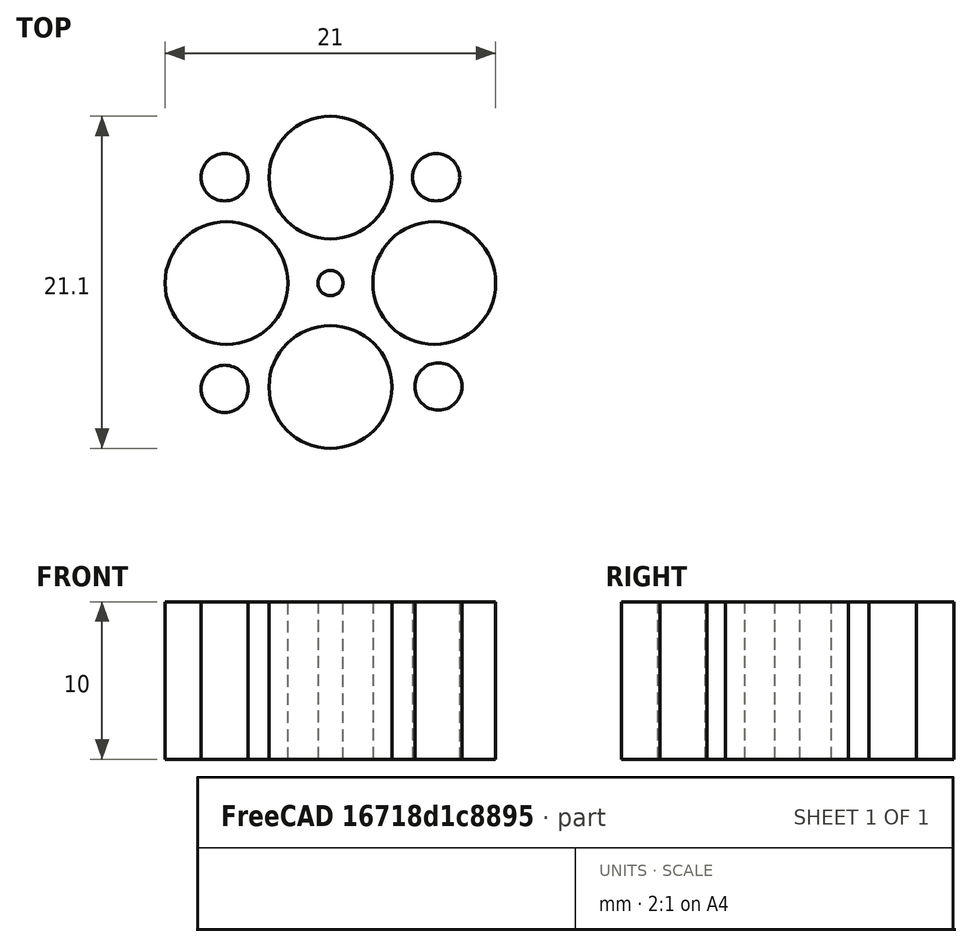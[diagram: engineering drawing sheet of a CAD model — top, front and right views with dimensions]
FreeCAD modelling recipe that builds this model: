
FCSTD DOCUMENT  (FreeCAD 0.19R0.19.2)
Label: 008
License: All rights reserved
LicenseURL: http://en.wikipedia.org/wiki/All_rights_reserved
objects: Sketcher::SketchObject×2, Part::Extrusion×1
note: 3 computed .brp shape members not serialized (recipe doc carries the construction recipe); baked Part::Feature solids carry a one-line shape summary decoded from their .brp

FEATURE [Sketcher::SketchObject] Sketch  label="holes"
  FullyConstrained = true
  sketch-geometry (9):
    g0: Circle CenterX=0 CenterY=0 CenterZ=0 NormalX=0 NormalY=0 NormalZ=1 AngleXU=0 Radius=0.8
    g1: Circle CenterX=0 CenterY=6.7 CenterZ=0 NormalX=0 NormalY=0 NormalZ=1 AngleXU=0 Radius=3.9
    g2: Circle CenterX=6.6 CenterY=0 CenterZ=0 NormalX=0 NormalY=0 NormalZ=1 AngleXU=0 Radius=3.9
    g3: Circle CenterX=-6.6 CenterY=0 CenterZ=0 NormalX=0 NormalY=0 NormalZ=1 AngleXU=0 Radius=3.9
    g4: Circle CenterX=0 CenterY=-6.6 CenterZ=0 NormalX=0 NormalY=0 NormalZ=1 AngleXU=0 Radius=3.9
    g5: Circle CenterX=6.71751 CenterY=6.71751 CenterZ=0 NormalX=0 NormalY=0 NormalZ=1 AngleXU=0 Radius=1.5
    g6: Circle CenterX=-6.71751 CenterY=-6.71751 CenterZ=0 NormalX=0 NormalY=0 NormalZ=1 AngleXU=0 Radius=1.5
    g7: Circle CenterX=-6.71751 CenterY=6.71751 CenterZ=0 NormalX=0 NormalY=0 NormalZ=1 AngleXU=0 Radius=1.5
    g8: Circle CenterX=6.86196 CenterY=-6.56989 CenterZ=0 NormalX=0 NormalY=0 NormalZ=1 AngleXU=0 Radius=1.5
  constraints (9):
    c: Block(g5)
    c: Block(g2)
    c: Block(g1)
    c: Block(g7)
    c: Block(g3)
    c: Block(g6)
    c: Block(g4)
    c: Block(g0)
    c: Block(g8)
FEATURE [Part::Extrusion] Extrude
  Base = -> Sketch
  Dir = (0,0,1)
  DirMode = 2
  FaceMakerClass = Part::FaceMakerBullseye
  LengthFwd = 10
  LengthRev = 0
  Solid = true
  Symmetric = false
FEATURE [Sketcher::SketchObject] Sketch001
  FullyConstrained = true
  Placement = pos=(0,0,0) rot=(0.57735,0.57735,0.57735;2.0944rad)
  sketch-geometry (33):
    g0: LineSegment StartX=1.6 StartY=4 StartZ=0 EndX=0 EndY=4 EndZ=0
    g1: Circle CenterX=12.5 CenterY=0.7 CenterZ=0 NormalX=0 NormalY=0 NormalZ=1 AngleXU=0 Radius=1
    g2: Circle CenterX=13.06 CenterY=0 CenterZ=0 NormalX=0 NormalY=0 NormalZ=1 AngleXU=0 Radius=1
    g3: Circle CenterX=12.5 CenterY=-0.7 CenterZ=0 NormalX=0 NormalY=0 NormalZ=1 AngleXU=0 Radius=1
    g4: BSplineCurve PolesCount=3 KnotsCount=2 Degree=2 IsPeriodic=0
    g5: GeomPoint X=12.5 Y=0.7 Z=0
    g6: GeomPoint X=12.5 Y=-0.7 Z=0
    g7: Circle CenterX=1.6 CenterY=4 CenterZ=0 NormalX=0 NormalY=0 NormalZ=1 AngleXU=0 Radius=1
    g8: Circle CenterX=1.96118 CenterY=1.73941 CenterZ=0 NormalX=0 NormalY=0 NormalZ=1 AngleXU=0 Radius=1
    g9: Circle CenterX=2.61896 CenterY=1.5 CenterZ=0 NormalX=0 NormalY=0 NormalZ=1 AngleXU=0 Radius=1
    g10: BSplineCurve PolesCount=3 KnotsCount=2 Degree=2 IsPeriodic=0
    g11: GeomPoint X=1.6 Y=4 Z=0
    g12: GeomPoint X=2.61896 Y=1.5 Z=0
    g13: LineSegment StartX=1.6 StartY=-4 StartZ=0 EndX=0 EndY=-4 EndZ=0
    g14: LineSegment StartX=0 StartY=-4 StartZ=0 EndX=0 EndY=4 EndZ=0
    g15: Circle CenterX=1.6 CenterY=-4 CenterZ=0 NormalX=0 NormalY=0 NormalZ=1 AngleXU=0 Radius=1
    g16: Circle CenterX=1.96118 CenterY=-1.73941 CenterZ=0 NormalX=0 NormalY=0 NormalZ=1 AngleXU=0 Radius=1
    g17: Circle CenterX=2.61896 CenterY=-1.5 CenterZ=0 NormalX=0 NormalY=0 NormalZ=1 AngleXU=0 Radius=1
    g18: BSplineCurve PolesCount=3 KnotsCount=2 Degree=2 IsPeriodic=0
    g19: GeomPoint X=1.6 Y=-4 Z=0
    g20: GeomPoint X=2.61896 Y=-1.5 Z=0
    g21: Circle CenterX=12.5 CenterY=0.7 CenterZ=0 NormalX=0 NormalY=0 NormalZ=1 AngleXU=0 Radius=1
    g22: Circle CenterX=3.81896 CenterY=1.5 CenterZ=0 NormalX=0 NormalY=0 NormalZ=1 AngleXU=0 Radius=1
    g23: Circle CenterX=2.61896 CenterY=1.5 CenterZ=0 NormalX=0 NormalY=0 NormalZ=1 AngleXU=0 Radius=1
    g24: BSplineCurve PolesCount=3 KnotsCount=2 Degree=2 IsPeriodic=0
    g25: GeomPoint X=12.5 Y=0.7 Z=0
    g26: GeomPoint X=2.61896 Y=1.5 Z=0
    g27: Circle CenterX=12.5 CenterY=-0.7 CenterZ=0 NormalX=0 NormalY=0 NormalZ=1 AngleXU=0 Radius=1
    g28: Circle CenterX=3.81896 CenterY=-1.5 CenterZ=0 NormalX=0 NormalY=0 NormalZ=1 AngleXU=0 Radius=1
    g29: Circle CenterX=2.61896 CenterY=-1.5 CenterZ=0 NormalX=0 NormalY=0 NormalZ=1 AngleXU=0 Radius=1
    g30: BSplineCurve PolesCount=3 KnotsCount=2 Degree=2 IsPeriodic=0
    g31: GeomPoint X=12.5 Y=-0.7 Z=0
    g32: GeomPoint X=2.61896 Y=-1.5 Z=0
  constraints (58):
    c: Horizontal(g0)
    c: Distance(g0) = 1.6
    c: Weight(g1) = 1
    c: Equal(g1,g2)
    c: Equal(g1,g3)
    c: InternalAlignment(g1,g4)
    c: InternalAlignment(g2,g4)
    c: InternalAlignment(g3,g4)
    c: InternalAlignment(g5,g4)
    c: InternalAlignment(g6,g4)
    c: Block(g4)
    c: Block(g0)
    c: Coincident(g10,g0)
    c: Weight(g7) = 1
    c: Equal(g7,g8)
    c: Equal(g7,g9)
    c: InternalAlignment(g7,g10)
    c: InternalAlignment(g8,g10)
    c: InternalAlignment(g9,g10)
    c: InternalAlignment(g11,g10)
    c: InternalAlignment(g12,g10)
    c: Horizontal(g13)
    c: Distance(g13) = 1.6
    c: Coincident(g14,g13)
    c: Coincident(g14,g0)
    c: Vertical(g14)
    c: Block(g13)
    c: Coincident(g18,g13)
    c: Weight(g15) = 1
    c: Equal(g15,g16)
    c: Equal(g15,g17)
    c: InternalAlignment(g15,g18)
    c: InternalAlignment(g16,g18)
    c: InternalAlignment(g17,g18)
    c: InternalAlignment(g19,g18)
    c: InternalAlignment(g20,g18)
    c: Block(g18)
    c: Block(g10)
    c: Coincident(g24,g4)
    c: Weight(g21) = 1
    c: Equal(g21,g22)
    c: Equal(g21,g23)
    c: InternalAlignment(g21,g24)
    c: InternalAlignment(g22,g24)
    c: InternalAlignment(g23,g24)
    c: InternalAlignment(g25,g24)
    c: InternalAlignment(g26,g24)
    c: Coincident(g30,g4)
    c: Weight(g27) = 1
    c: Equal(g27,g28)
    c: Equal(g27,g29)
    c: InternalAlignment(g27,g30)
    c: InternalAlignment(g28,g30)
    c: InternalAlignment(g29,g30)
    c: InternalAlignment(g31,g30)
    c: InternalAlignment(g32,g30)
    c: Block(g24)
    c: Block(g30)
